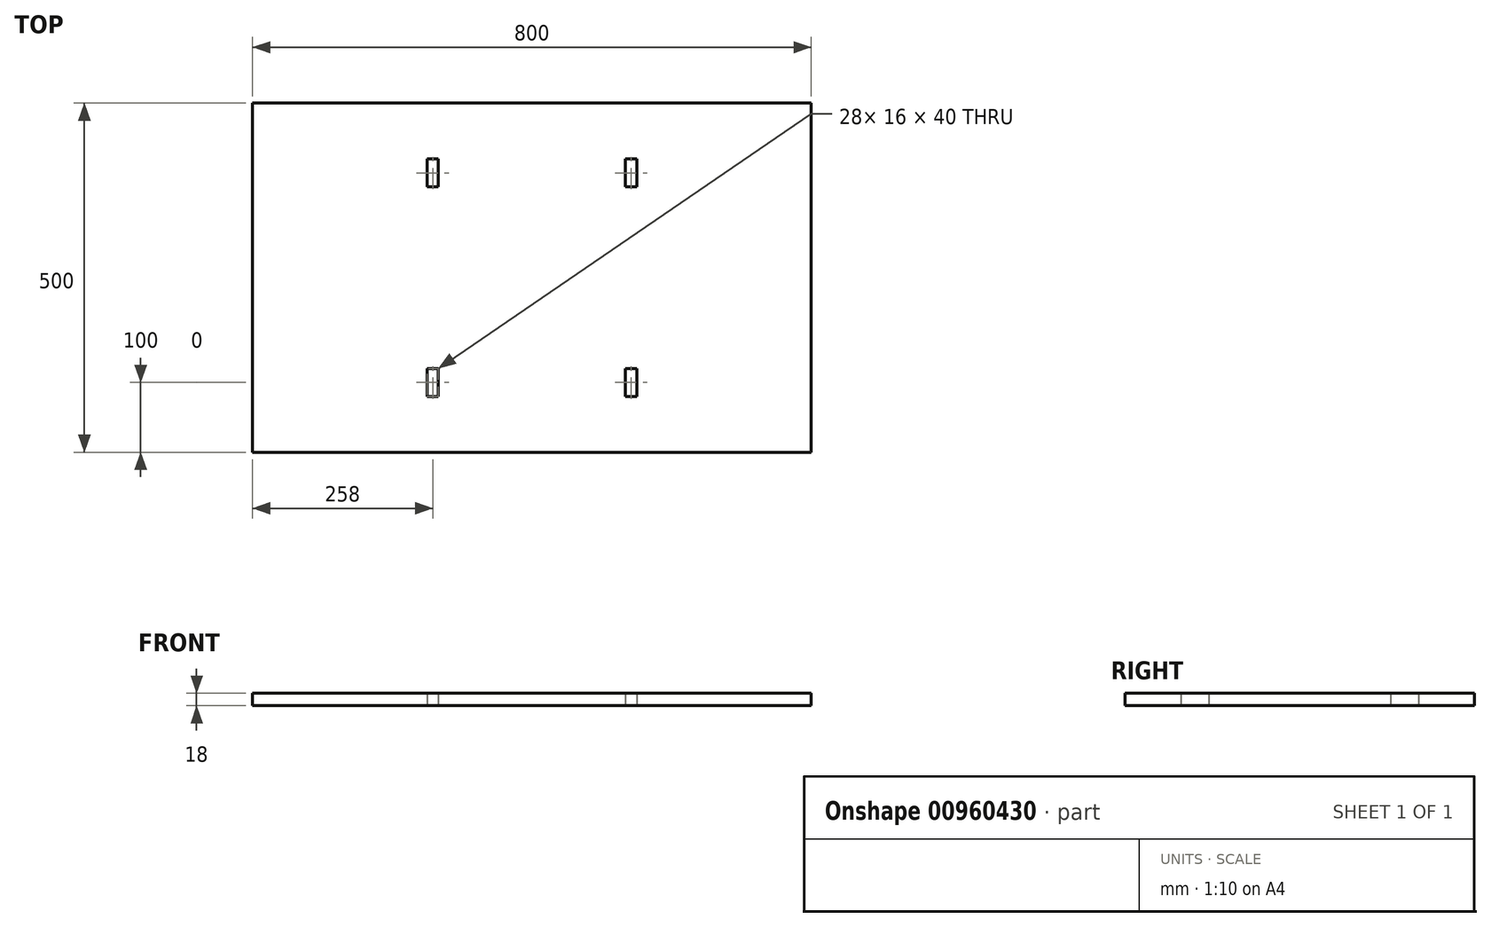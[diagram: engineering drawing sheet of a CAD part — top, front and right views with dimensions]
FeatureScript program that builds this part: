
annotation { "Feature Type Name" : "Feature", "Feature Type Description" : "" }
export const myFeature = defineFeature(function(context is Context, id is Id, definition is map)
    precondition{}
    {
        {
            var Q0;
            Q0=qCreatedBy(makeId("Top.planeOp"),FACE);
            var sketch = newSketch(context, id + "F0", { "sketchPlane" : qUnion([Q0])});
            skLineSegment(sketch, "E0.bottom", {"start": v(400, -250) * mm, "end": v(-400, -250) * mm});
            skLineSegment(sketch, "E0.top", {"start": v(400, 250) * mm, "end": v(-400, 250) * mm});
            skLineSegment(sketch, "E0.left", {"start": v(400, -250) * mm, "end": v(400, 250) * mm});
            skLineSegment(sketch, "E0.right", {"start": v(-400, -250) * mm, "end": v(-400, 250) * mm});
            skPoint(sketch, "E0.middle", {"position": v(0, 0) * mm});
            skLineSegment(sketch, "E1", {"start": v(-456.7, 0) * mm, "end": v(464.45, 0) * mm, "construction": true});
            skLineSegment(sketch, "E2", {"start": v(0, 314.86) * mm, "end": v(0, -306.64) * mm, "construction": true});
            skLineSegment(sketch, "E3.bottom", {"start": v(134, 170) * mm, "end": v(150, 170) * mm});
            skLineSegment(sketch, "E3.top", {"start": v(134, 130) * mm, "end": v(150, 130) * mm});
            skLineSegment(sketch, "E3.left", {"start": v(134, 170) * mm, "end": v(134, 130) * mm});
            skLineSegment(sketch, "E3.right", {"start": v(150, 170) * mm, "end": v(150, 130) * mm});
            skLineSegment(sketch, "E4.MirrorCS", {"start": v(-134, 130) * mm, "end": v(-150, 130) * mm});
            skLineSegment(sketch, "E5.MirrorCS", {"start": v(-134, 170) * mm, "end": v(-134, 130) * mm});
            skLineSegment(sketch, "E6.MirrorCS", {"start": v(-134, 170) * mm, "end": v(-150, 170) * mm});
            skLineSegment(sketch, "E7.MirrorCS", {"start": v(-150, 170) * mm, "end": v(-150, 130) * mm});
            skLineSegment(sketch, "E8.MirrorCS", {"start": v(-134, -170) * mm, "end": v(-134, -130) * mm});
            skLineSegment(sketch, "E9.MirrorCS", {"start": v(-150, -170) * mm, "end": v(-150, -130) * mm});
            skLineSegment(sketch, "E10.MirrorCS", {"start": v(-134, -170) * mm, "end": v(-150, -170) * mm});
            skLineSegment(sketch, "E11.MirrorCS", {"start": v(-134, -130) * mm, "end": v(-150, -130) * mm});
            skLineSegment(sketch, "E12.MirrorCS", {"start": v(150, -170) * mm, "end": v(150, -130) * mm});
            skLineSegment(sketch, "E13.MirrorCS", {"start": v(134, -170) * mm, "end": v(134, -130) * mm});
            skLineSegment(sketch, "E14.MirrorCS", {"start": v(134, -170) * mm, "end": v(150, -170) * mm});
            skLineSegment(sketch, "E15.MirrorCS", {"start": v(134, -130) * mm, "end": v(150, -130) * mm});
            skSolve(sketch);
        }
        {
            var Q0;
            Q0 = qSketchRegion(id + "F0", true);
            extrude(context, id + "F1", {"entities" : qUnion([Q0]), "depth" : 18 * mm, "offsetDistance" : 25 * mm});
        }
    });
